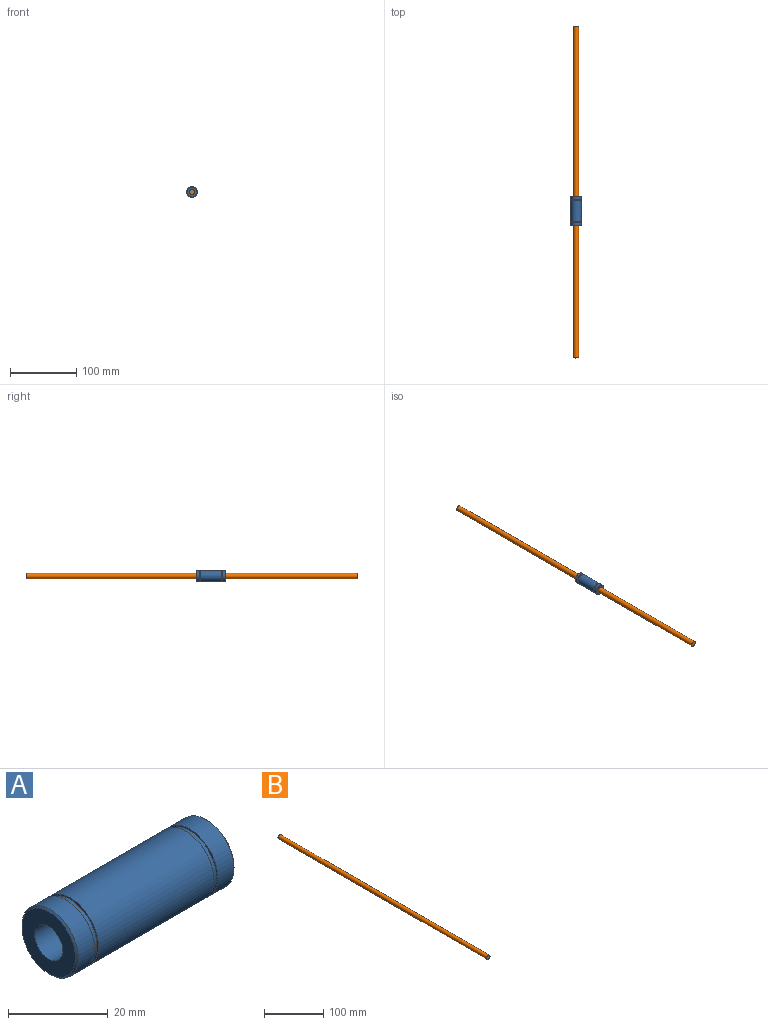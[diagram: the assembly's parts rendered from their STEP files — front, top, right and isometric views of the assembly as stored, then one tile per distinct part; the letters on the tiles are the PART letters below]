
ASSEMBLY  parts=2 mates=1
PART A: 14 faces, bbox 45x16x16 mm
  f0: cylinder r=8mm len=32.8mm, axis (-1,0,0), area 1648.7mm2, adj f1,f13
  f1: plane 16x16mm, normal (-1,0,0), area 19.6mm2, adj f0,f2
  f2: cylinder r=7.6mm len=15.2mm, axis (-1,0,0), area 52.5mm2, adj f1,f3
  f3: plane 16x16mm, normal (1,0,0), area 19.6mm2, adj f2,f4
  f4: cylinder r=8mm len=16mm, axis (-1,0,0), area 231.2mm2, adj f3,f5
  f5: cone r=8mm half-angle=45deg, axis (1,0,0), area 27.7mm2, adj f4,f6
  f6: plane 15.2x15.2mm, normal (-1,0,0), area 131.2mm2, adj f5,f7
  f7: cylinder r=4mm len=45mm, axis (-1,0,0), area 1131mm2, adj f6,f8
  f8: plane 15.2x15.2mm, normal (1,0,0), area 131.2mm2, adj f7,f9
  f9: cone r=8mm half-angle=45deg, axis (-1,0,0), area 27.7mm2, adj f8,f10
  f10: cylinder r=8mm len=16mm, axis (-1,0,0), area 231.2mm2, adj f9,f11
  f11: plane 16x16mm, normal (-1,0,0), area 19.6mm2, adj f10,f12
  f12: cylinder r=7.6mm len=15.2mm, axis (-1,0,0), area 52.5mm2, adj f11,f13
  f13: plane 16x16mm, normal (1,0,0), area 19.6mm2, adj f0,f12
PART B: 3 faces, bbox 8x500x8 mm
  f0: cylinder r=4mm len=500mm, axis (0,1,0), area 12566.4mm2, adj f1,f2
  f1: plane 8x8mm, normal (0,-1,0), area 50.3mm2, adj f0
  f2: plane 8x8mm, normal (0,1,0), area 50.3mm2, adj f0
PLACE A rot(axis=(0.03,-0.03,-1),90deg) t=(0,-278.58,0)mm
PLACE B at identity fixed
MATE cylindrical A.f0 <-> B.f0  axis (0,-1,0) through (0,-301.08,0)mm
